# Revit family: NBS_BetafenceLimited_MtlMeshPnlFncngSym_PaladinFX-Twilfix
name_source: partatom
category: Site
revit_build: Autodesk Revit 2017 (Build: 20171027_0315(x64)
units: mm (PartAtom-declared; Revit-internal decimal feet)

## family parameters
Cut with Voids When Loaded = No
Part Type = Normal
Round Connector Dimension = Use Diameter
Shared = No

## types (1)
- Paladin FX + Twilfix
    Applications = Company premises, public spaces, schools, retail, factories, airports, utilities
    AssetType = Fixed
    BIMObjectName = NBS_BetafenceLimited_MetalMeshPanelFencingSystem_PaladinFX-Twilfix
    Category = Ss_25_14_67_51:Metal mesh panel fencing systems
    Color = Green (RAL 6005), black (RAL 9005)
    Description = Perimeter security
    Diameter = 0 mm  [stored 0 ft]
    DurationUnit = year
    Fixings = Metal, plastic
    FoundationMaterial = NBS_Concept
    Gradient01Maximum = 3.31%
    Gradient01PostAxisDistance = 3025 mm  [stored 9.92454 ft]
    Gradient02Maximum = 5.09%
    Gradient02PostAxisDistance = 1965 mm
    Gradient03Maximum = 7.03%
    Gradient03PostAxisDistance = 1422 mm
    Gradient04Maximum = 9.37%
    Gradient04PostAxisDistance = 1067 mm
    GradientMaximumPostAxisDistance = 1067 mm
    Height = 2400 mm
    IfcExportAs = IfcWallType
    IfcExportType = NOTDEFINED
    IsExternal = Yes
    ManufacturerName = Betafence Limited
    ManufacturerURL = www.betafence.co.uk
    MaximumIncline = 9.20%
    ModelReference = Paladin FX Twilfix
    NBSCertification = www.nationalbimlibrary.com/cert/5sj2y0wb
    NBSDescription = Metal mesh panel fencing system
    NBSReference = 25-20-30/145
    Name = MetalMeshPanelFencingSystem_PaladinFXTwilfix_BetafenceLimited
    NominalHeight = 2400 mm
    NominalLength = 0 mm  [stored 0 ft]
    NominalWidth = 3050 mm
    PanelElevationAboveFoundation = 270 mm  [stored 0.885827 ft]
    PanelHeight = 2400 mm
    PanelMaterial = NBS_BetafenceLimited_MtlMeshPnlFncngSym_PaladinFX_Panel
    PanelOffsetFromPost = 12 mm  [stored 0.0393701 ft]
    PanelOffsetFromPostCL = 75 mm  [stored 0.246063 ft]
    PanelSizeOptions = 3023 x 1200 mm, 3023 x 1800 mm, 3023 x 2000 mm, 3023 x 2400 mm
    PanelThickness = 45 mm  [stored 0.147638 ft]
    PostFoundations = Installation guides available on request
    PostHeightAboveGround = 2470 mm  [stored 8.10367 ft]
    PostHeightBelowGround = 200 mm  [stored 0.656168 ft]
    PostMaterial = NBS_Concept
    PostThickness = 60 mm  [stored 0.19685 ft]
    PostWidth = 60 mm  [stored 0.19685 ft]
    Posts = Twilfix
    ProductInformation = www.betafence.co.uk/en/paladin®-fx
    SecurityLevel = General purpose and security
    StandardPostAxisDistance = 3050 mm
    SystemAccessories = Concrete plate holder, cranked extension arm and connection piece or welded cranked arms, security devices
    Uniclass2015Code = Ss_25_14_67_51
    Uniclass2015Title = Metal mesh panel fencing systems
    Uniclass2015Version = Systems v1.13
    Version = 3
    WarrantyDurationUnit = year

note: [stored X ft] marks values corroborated as IEEE doubles in the binary element streams (Revit-internal decimal feet)

## geometry (parser evidence)
native form markers: Sweep x8
no freeform markers — native parametric forms only
